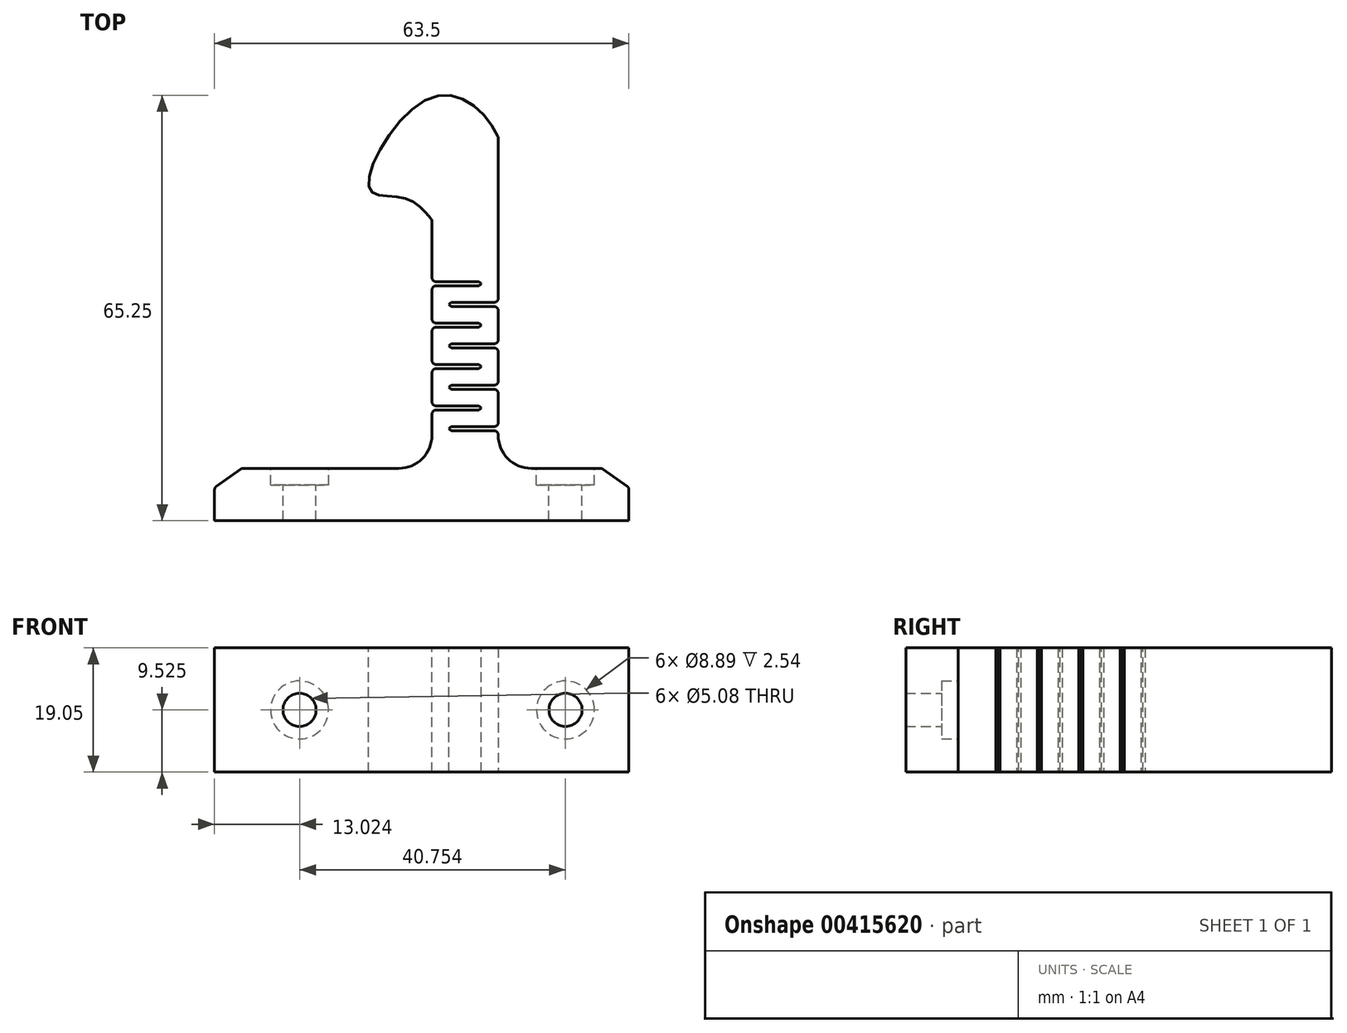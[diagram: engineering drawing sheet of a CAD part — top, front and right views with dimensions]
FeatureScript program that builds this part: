
annotation { "Feature Type Name" : "Feature", "Feature Type Description" : "" }
export const myFeature = defineFeature(function(context is Context, id is Id, definition is map)
    precondition{}
    {
        {
            var Q0;
            Q0=qCreatedBy(makeId("Top.planeOp"),FACE);
            var sketch = newSketch(context, id + "F0", { "sketchPlane" : qUnion([Q0])});
            skLineSegment(sketch, "E0", {"start": v(0, 0) * mm, "end": v(63.5, 0) * mm});
            skLineSegment(sketch, "E1", {"start": v(63.5, 0) * mm, "end": v(63.5, 5.08) * mm});
            skLineSegment(sketch, "E2", {"start": v(63.5, 5.08) * mm, "end": v(59.35, 8.01) * mm});
            skLineSegment(sketch, "E3", {"start": v(0, 0) * mm, "end": v(0, 5.08) * mm});
            skLineSegment(sketch, "E4", {"start": v(0, 5.08) * mm, "end": v(4.15, 8.01) * mm});
            skLineSegment(sketch, "E5", {"start": v(4.15, 8.01) * mm, "end": v(59.35, 8.01) * mm});
            skLineSegment(sketch, "E6", {"start": v(33.32, 8.01) * mm, "end": v(33.32, 46.11) * mm});
            skLineSegment(sketch, "E7", {"start": v(43.48, 8.01) * mm, "end": v(43.48, 58.81) * mm});
            skFitSpline(sketch, "E8", {"points": [v(33.32, 46.11) * mm, v(28.79, 49.55) * mm, v(23.73, 50.95) * mm, v(33.32, 64.92) * mm, v(43.48, 58.81) * mm, v(43.48, 47.98) * mm], "startDerivative": vector(-22.66, 29.78) * mm, "endDerivative": vector(-11.05, -50.67) * mm});
            skLineSegment(sketch, "E9.bottom", {"start": v(33.32, 36.01) * mm, "end": v(40.94, 36.01) * mm});
            skLineSegment(sketch, "E9.top", {"start": v(33.32, 36.65) * mm, "end": v(40.94, 36.65) * mm});
            skLineSegment(sketch, "E9.left", {"start": v(33.32, 36.01) * mm, "end": v(33.32, 36.65) * mm});
            skLineSegment(sketch, "E9.right", {"start": v(40.94, 36.01) * mm, "end": v(40.94, 36.65) * mm});
            skLineSegment(sketch, "E10", {"start": v(41.84, 33.47) * mm, "end": v(43.48, 33.47) * mm});
            skLineSegment(sketch, "E11.bottom", {"start": v(43.48, 33.47) * mm, "end": v(35.86, 33.47) * mm});
            skLineSegment(sketch, "E11.top", {"start": v(43.48, 32.84) * mm, "end": v(35.86, 32.84) * mm});
            skLineSegment(sketch, "E11.left", {"start": v(43.48, 33.47) * mm, "end": v(43.48, 32.84) * mm});
            skLineSegment(sketch, "E11.right", {"start": v(35.86, 33.47) * mm, "end": v(35.86, 32.84) * mm});
            skLineSegment(sketch, "E12", {"start": v(33.32, 36.01) * mm, "end": v(33.32, 30.3) * mm});
            skLineSegment(sketch, "E13", {"start": v(43.48, 32.84) * mm, "end": v(43.48, 27.12) * mm});
            skLineSegment(sketch, "E14.bottom", {"start": v(33.32, 30.3) * mm, "end": v(40.94, 30.3) * mm});
            skLineSegment(sketch, "E14.top", {"start": v(33.32, 29.66) * mm, "end": v(40.94, 29.66) * mm});
            skLineSegment(sketch, "E14.left", {"start": v(33.32, 30.3) * mm, "end": v(33.32, 29.66) * mm});
            skLineSegment(sketch, "E14.right", {"start": v(40.94, 30.3) * mm, "end": v(40.94, 29.66) * mm});
            skLineSegment(sketch, "E15.bottom", {"start": v(43.48, 27.12) * mm, "end": v(35.86, 27.12) * mm});
            skLineSegment(sketch, "E15.top", {"start": v(43.48, 26.49) * mm, "end": v(35.86, 26.49) * mm});
            skLineSegment(sketch, "E15.left", {"start": v(43.48, 27.12) * mm, "end": v(43.48, 26.49) * mm});
            skLineSegment(sketch, "E15.right", {"start": v(35.86, 27.12) * mm, "end": v(35.86, 26.49) * mm});
            skLineSegment(sketch, "E16", {"start": v(33.32, 29.66) * mm, "end": v(33.32, 23.95) * mm});
            skLineSegment(sketch, "E17", {"start": v(43.48, 26.49) * mm, "end": v(43.48, 20.77) * mm});
            skLineSegment(sketch, "E18.bottom", {"start": v(33.32, 23.95) * mm, "end": v(40.94, 23.95) * mm});
            skLineSegment(sketch, "E18.top", {"start": v(33.32, 23.31) * mm, "end": v(40.94, 23.31) * mm});
            skLineSegment(sketch, "E18.left", {"start": v(33.32, 23.95) * mm, "end": v(33.32, 23.31) * mm});
            skLineSegment(sketch, "E18.right", {"start": v(40.94, 23.95) * mm, "end": v(40.94, 23.31) * mm});
            skLineSegment(sketch, "E19.bottom", {"start": v(43.48, 20.77) * mm, "end": v(35.86, 20.77) * mm});
            skLineSegment(sketch, "E19.top", {"start": v(43.48, 20.14) * mm, "end": v(35.86, 20.14) * mm});
            skLineSegment(sketch, "E19.left", {"start": v(43.48, 20.77) * mm, "end": v(43.48, 20.14) * mm});
            skLineSegment(sketch, "E19.right", {"start": v(35.86, 20.77) * mm, "end": v(35.86, 20.14) * mm});
            skLineSegment(sketch, "E20", {"start": v(33.32, 23.31) * mm, "end": v(33.32, 17.6) * mm});
            skLineSegment(sketch, "E21", {"start": v(43.48, 20.14) * mm, "end": v(43.48, 14.42) * mm});
            skLineSegment(sketch, "E22.bottom", {"start": v(33.32, 17.6) * mm, "end": v(40.94, 17.6) * mm});
            skLineSegment(sketch, "E22.top", {"start": v(33.32, 16.96) * mm, "end": v(40.94, 16.96) * mm});
            skLineSegment(sketch, "E22.left", {"start": v(33.32, 17.6) * mm, "end": v(33.32, 16.96) * mm});
            skLineSegment(sketch, "E22.right", {"start": v(40.94, 17.6) * mm, "end": v(40.94, 16.96) * mm});
            skLineSegment(sketch, "E23.bottom", {"start": v(43.48, 14.42) * mm, "end": v(35.86, 14.42) * mm});
            skLineSegment(sketch, "E23.top", {"start": v(43.48, 13.79) * mm, "end": v(35.86, 13.79) * mm});
            skLineSegment(sketch, "E23.left", {"start": v(43.48, 14.42) * mm, "end": v(43.48, 13.79) * mm});
            skLineSegment(sketch, "E23.right", {"start": v(35.86, 14.42) * mm, "end": v(35.86, 13.79) * mm});
            skLineSegment(sketch, "E24", {"start": v(43.48, 36.01) * mm, "end": v(43.48, 33.47) * mm});
            skSolve(sketch);
        }
        {
            var Q0;
            Q0=makeQuery(id+"F0.imprint","IMPRINT",FACE,{"disambiguationData":[TD([[makeQuery(id+"F0.imprint","IMPRINT",EDGE,{"derivedFrom":sQuery(id+"F0.wireOp",EDGE,"E0")}),1.0]])]});
            var Q1;
            {var subQ0=sQuery(id+"F0.wireOp",EDGE,"E8");var subQ1=sQuery(id+"F0.wireOp",EDGE,"E7");var subQ2=makeQuery(id+"F0.imprint","INTERSECT",VERTEX,{"disambiguationData":[OD(0.0)],"derivedFrom":[subQ1,subQ0]});Q1=makeQuery(id+"F0.imprint","IMPRINT",FACE,{"disambiguationData":[TD([[makeQuery(id+"F0.imprint","IMPRINT",EDGE,{"disambiguationData":[TD([[subQ2,1.0]])],"derivedFrom":subQ1}),-1.0]])]});}
            var Q2;
            Q2=makeQuery(id+"F0.imprint","IMPRINT",FACE,{"disambiguationData":[TD([[makeQuery(id+"F0.imprint","IMPRINT",EDGE,{"derivedFrom":sQuery(id+"F0.wireOp",EDGE,"E9.bottom")}),-1.0]])]});
            extrude(context, id + "F1", {"entities" : qUnion([Q0, Q1, Q2]), "depth" : 19.05 * mm});
        }
        {
            var Q0;
            Q0=makeQuery(id+"F1.opExtrude","SWEPT_EDGE",EDGE,{"disambiguationData":[OSD([sQuery(id+"F0.wireOp",EDGE,"E5"),sQuery(id+"F0.wireOp",EDGE,"E6")])]});
            var Q1;
            Q1=makeQuery(id+"F1.opExtrude","SWEPT_EDGE",EDGE,{"disambiguationData":[OSD([sQuery(id+"F0.wireOp",EDGE,"E5"),sQuery(id+"F0.wireOp",EDGE,"E7")])]});
            fillet(context, id + "F2", {"entities" : qUnion([Q0, Q1]), "radius" : 5.08 * mm, "tangentPropagation" : true, "allowEdgeOverflow" : false});
        }
        {
            var Q0;
            {var subQ0=sQuery(id+"F0.wireOp",EDGE,"E5");Q0=makeQuery(id+"F1.opExtrude","SWEPT_FACE",FACE,{"disambiguationData":[OSD([subQ0]),TDD([makeQuery(id+"F0.imprint","IMPRINT",EDGE,{"disambiguationData":[TD([[makeQuery(id+"F0.imprint","INTERSECT",VERTEX,{"derivedFrom":[sQuery(id+"F0.wireOp",EDGE,"E4"),subQ0]}),-1.0]])],"derivedFrom":subQ0})])]});}
            var sketch = newSketch(context, id + "F3", { "sketchPlane" : qUnion([Q0])});
            skCircle(sketch, "E25", {"center": v(-13.02, 9.53) * mm, "radius": 2.54 * mm});
            skPoint(sketch, "E25.centerSnap0", {"position": v(-4.15, 9.53) * mm});
            skCircle(sketch, "E26", {"center": v(-13.02, 9.53) * mm, "radius": 4.45 * mm});
            skCircle(sketch, "E27", {"center": v(-53.78, 9.53) * mm, "radius": 2.54 * mm});
            skCircle(sketch, "E28", {"center": v(-53.78, 9.53) * mm, "radius": 4.45 * mm});
            skSolve(sketch);
        }
        {
            var Q0;
            Q0 = qSketchRegion(id + "F3", true);
            extrude(context, id + "F4", {"entities" : qUnion([Q0]), "operationType" : NewBodyOperationType.REMOVE, "oppositeDirection" : true, "depth" : 2.54 * mm});
        }
        {
            var Q0;
            {var subQ0=sQuery(id+"F0.wireOp",EDGE,"E5");Q0=makeQuery(id+"F4.boolean.opBoolean","SPLIT",FACE,{"disambiguationData":[TD([makeQuery(id+"F4.opExtrude","SWEPT_FACE",FACE,{"disambiguationData":[OSD([sQuery(id+"F3.wireOp",EDGE,"E25")])]})])],"derivedFrom":makeQuery(id+"F1.opExtrude","SWEPT_FACE",FACE,{"disambiguationData":[OSD([subQ0]),TDD([makeQuery(id+"F0.imprint","IMPRINT",EDGE,{"disambiguationData":[TD([[makeQuery(id+"F0.imprint","INTERSECT",VERTEX,{"derivedFrom":[sQuery(id+"F0.wireOp",EDGE,"E4"),subQ0]}),-1.0]])],"derivedFrom":subQ0})])]})});}
            var Q1;
            {var subQ0=sQuery(id+"F0.wireOp",EDGE,"E5");Q1=makeQuery(id+"F4.boolean.opBoolean","SPLIT",FACE,{"disambiguationData":[TD([makeQuery(id+"F4.opExtrude","SWEPT_FACE",FACE,{"disambiguationData":[OSD([sQuery(id+"F3.wireOp",EDGE,"E27")])]})])],"derivedFrom":makeQuery(id+"F1.opExtrude","SWEPT_FACE",FACE,{"disambiguationData":[OSD([subQ0]),TDD([makeQuery(id+"F0.imprint","IMPRINT",EDGE,{"disambiguationData":[TD([[makeQuery(id+"F0.imprint","INTERSECT",VERTEX,{"derivedFrom":[sQuery(id+"F0.wireOp",EDGE,"E2"),subQ0]}),1.0]])],"derivedFrom":subQ0})])]})});}
            extrude(context, id + "F5", {"entities" : qUnion([Q0, Q1]), "operationType" : NewBodyOperationType.REMOVE, "oppositeDirection" : true, "depth" : 25.4 * mm});
        }
        {
            var Q0;
            Q0=makeQuery(id+"F1.opExtrude","SWEPT_EDGE",EDGE,{"disambiguationData":[OSD([sQuery(id+"F0.wireOp",EDGE,"E21"),sQuery(id+"F0.wireOp",EDGE,"E23.bottom"),sQuery(id+"F0.wireOp",EDGE,"E23.left")])]});
            var Q1;
            Q1=makeQuery(id+"F1.opExtrude","SWEPT_EDGE",EDGE,{"disambiguationData":[OSD([sQuery(id+"F0.wireOp",EDGE,"E19.top"),sQuery(id+"F0.wireOp",EDGE,"E19.left"),sQuery(id+"F0.wireOp",EDGE,"E21")])]});
            var Q2;
            Q2=makeQuery(id+"F1.opExtrude","SWEPT_EDGE",EDGE,{"disambiguationData":[OSD([sQuery(id+"F0.wireOp",EDGE,"E17"),sQuery(id+"F0.wireOp",EDGE,"E19.bottom"),sQuery(id+"F0.wireOp",EDGE,"E19.left")])]});
            var Q3;
            Q3=makeQuery(id+"F1.opExtrude","SWEPT_EDGE",EDGE,{"disambiguationData":[OSD([sQuery(id+"F0.wireOp",EDGE,"E15.top"),sQuery(id+"F0.wireOp",EDGE,"E15.left"),sQuery(id+"F0.wireOp",EDGE,"E17")])]});
            var Q4;
            Q4=makeQuery(id+"F1.opExtrude","SWEPT_EDGE",EDGE,{"disambiguationData":[OSD([sQuery(id+"F0.wireOp",EDGE,"E13"),sQuery(id+"F0.wireOp",EDGE,"E15.bottom"),sQuery(id+"F0.wireOp",EDGE,"E15.left")])]});
            var Q5;
            Q5=makeQuery(id+"F1.opExtrude","SWEPT_EDGE",EDGE,{"disambiguationData":[OSD([sQuery(id+"F0.wireOp",EDGE,"E11.top"),sQuery(id+"F0.wireOp",EDGE,"E11.left"),sQuery(id+"F0.wireOp",EDGE,"E13")])]});
            var Q6;
            Q6=makeQuery(id+"F1.opExtrude","SWEPT_EDGE",EDGE,{"disambiguationData":[OSD([sQuery(id+"F0.wireOp",EDGE,"E7"),sQuery(id+"F0.wireOp",EDGE,"E11.bottom"),sQuery(id+"F0.wireOp",EDGE,"E11.left")])]});
            var Q7;
            Q7=makeQuery(id+"F1.opExtrude","SWEPT_EDGE",EDGE,{"disambiguationData":[OSD([sQuery(id+"F0.wireOp",EDGE,"E6"),sQuery(id+"F0.wireOp",EDGE,"E9.top"),sQuery(id+"F0.wireOp",EDGE,"E9.left")])]});
            var Q8;
            Q8=makeQuery(id+"F1.opExtrude","SWEPT_EDGE",EDGE,{"disambiguationData":[OSD([sQuery(id+"F0.wireOp",EDGE,"E9.bottom"),sQuery(id+"F0.wireOp",EDGE,"E9.left"),sQuery(id+"F0.wireOp",EDGE,"E12")])]});
            var Q9;
            Q9=makeQuery(id+"F1.opExtrude","SWEPT_EDGE",EDGE,{"disambiguationData":[OSD([sQuery(id+"F0.wireOp",EDGE,"E12"),sQuery(id+"F0.wireOp",EDGE,"E14.bottom"),sQuery(id+"F0.wireOp",EDGE,"E14.left")])]});
            var Q10;
            Q10=makeQuery(id+"F1.opExtrude","SWEPT_EDGE",EDGE,{"disambiguationData":[OSD([sQuery(id+"F0.wireOp",EDGE,"E14.top"),sQuery(id+"F0.wireOp",EDGE,"E14.left"),sQuery(id+"F0.wireOp",EDGE,"E16")])]});
            var Q11;
            Q11=makeQuery(id+"F1.opExtrude","SWEPT_EDGE",EDGE,{"disambiguationData":[OSD([sQuery(id+"F0.wireOp",EDGE,"E16"),sQuery(id+"F0.wireOp",EDGE,"E18.bottom"),sQuery(id+"F0.wireOp",EDGE,"E18.left")])]});
            var Q12;
            Q12=makeQuery(id+"F1.opExtrude","SWEPT_EDGE",EDGE,{"disambiguationData":[OSD([sQuery(id+"F0.wireOp",EDGE,"E18.top"),sQuery(id+"F0.wireOp",EDGE,"E18.left"),sQuery(id+"F0.wireOp",EDGE,"E20")])]});
            var Q13;
            Q13=makeQuery(id+"F1.opExtrude","SWEPT_EDGE",EDGE,{"disambiguationData":[OSD([sQuery(id+"F0.wireOp",EDGE,"E20"),sQuery(id+"F0.wireOp",EDGE,"E22.bottom"),sQuery(id+"F0.wireOp",EDGE,"E22.left")])]});
            var Q14;
            Q14=makeQuery(id+"F1.opExtrude","SWEPT_EDGE",EDGE,{"disambiguationData":[OSD([sQuery(id+"F0.wireOp",EDGE,"E6"),sQuery(id+"F0.wireOp",EDGE,"E22.top"),sQuery(id+"F0.wireOp",EDGE,"E22.left")])]});
            var Q15;
            Q15=makeQuery(id+"F1.opExtrude","SWEPT_EDGE",EDGE,{"disambiguationData":[OSD([sQuery(id+"F0.wireOp",EDGE,"E9.bottom"),sQuery(id+"F0.wireOp",EDGE,"E9.right")])]});
            var Q16;
            Q16=makeQuery(id+"F1.opExtrude","SWEPT_EDGE",EDGE,{"disambiguationData":[OSD([sQuery(id+"F0.wireOp",EDGE,"E14.top"),sQuery(id+"F0.wireOp",EDGE,"E14.right")])]});
            var Q17;
            Q17=makeQuery(id+"F1.opExtrude","SWEPT_EDGE",EDGE,{"disambiguationData":[OSD([sQuery(id+"F0.wireOp",EDGE,"E18.top"),sQuery(id+"F0.wireOp",EDGE,"E18.right")])]});
            var Q18;
            Q18=makeQuery(id+"F1.opExtrude","SWEPT_EDGE",EDGE,{"disambiguationData":[OSD([sQuery(id+"F0.wireOp",EDGE,"E22.top"),sQuery(id+"F0.wireOp",EDGE,"E22.right")])]});
            var Q19;
            Q19=makeQuery(id+"F1.opExtrude","SWEPT_EDGE",EDGE,{"disambiguationData":[OSD([sQuery(id+"F0.wireOp",EDGE,"E22.bottom"),sQuery(id+"F0.wireOp",EDGE,"E22.right")])]});
            var Q20;
            Q20=makeQuery(id+"F1.opExtrude","SWEPT_EDGE",EDGE,{"disambiguationData":[OSD([sQuery(id+"F0.wireOp",EDGE,"E18.bottom"),sQuery(id+"F0.wireOp",EDGE,"E18.right")])]});
            var Q21;
            Q21=makeQuery(id+"F1.opExtrude","SWEPT_EDGE",EDGE,{"disambiguationData":[OSD([sQuery(id+"F0.wireOp",EDGE,"E14.bottom"),sQuery(id+"F0.wireOp",EDGE,"E14.right")])]});
            var Q22;
            Q22=makeQuery(id+"F1.opExtrude","SWEPT_EDGE",EDGE,{"disambiguationData":[OSD([sQuery(id+"F0.wireOp",EDGE,"E9.top"),sQuery(id+"F0.wireOp",EDGE,"E9.right")])]});
            var Q23;
            Q23=makeQuery(id+"F1.opExtrude","SWEPT_EDGE",EDGE,{"disambiguationData":[OSD([sQuery(id+"F0.wireOp",EDGE,"E11.top"),sQuery(id+"F0.wireOp",EDGE,"E11.right")])]});
            var Q24;
            Q24=makeQuery(id+"F1.opExtrude","SWEPT_EDGE",EDGE,{"disambiguationData":[OSD([sQuery(id+"F0.wireOp",EDGE,"E15.top"),sQuery(id+"F0.wireOp",EDGE,"E15.right")])]});
            var Q25;
            Q25=makeQuery(id+"F1.opExtrude","SWEPT_EDGE",EDGE,{"disambiguationData":[OSD([sQuery(id+"F0.wireOp",EDGE,"E19.top"),sQuery(id+"F0.wireOp",EDGE,"E19.right")])]});
            var Q26;
            Q26=makeQuery(id+"F1.opExtrude","SWEPT_EDGE",EDGE,{"disambiguationData":[OSD([sQuery(id+"F0.wireOp",EDGE,"E23.top"),sQuery(id+"F0.wireOp",EDGE,"E23.right")])]});
            var Q27;
            Q27=makeQuery(id+"F1.opExtrude","SWEPT_EDGE",EDGE,{"disambiguationData":[OSD([sQuery(id+"F0.wireOp",EDGE,"E23.bottom"),sQuery(id+"F0.wireOp",EDGE,"E23.right")])]});
            var Q28;
            Q28=makeQuery(id+"F1.opExtrude","SWEPT_EDGE",EDGE,{"disambiguationData":[OSD([sQuery(id+"F0.wireOp",EDGE,"E19.bottom"),sQuery(id+"F0.wireOp",EDGE,"E19.right")])]});
            var Q29;
            Q29=makeQuery(id+"F1.opExtrude","SWEPT_EDGE",EDGE,{"disambiguationData":[OSD([sQuery(id+"F0.wireOp",EDGE,"E15.bottom"),sQuery(id+"F0.wireOp",EDGE,"E15.right")])]});
            var Q30;
            Q30=makeQuery(id+"F1.opExtrude","SWEPT_EDGE",EDGE,{"disambiguationData":[OSD([sQuery(id+"F0.wireOp",EDGE,"E11.bottom"),sQuery(id+"F0.wireOp",EDGE,"E11.right")])]});
            var Q31;
            Q31=makeQuery(id+"F1.opExtrude","SWEPT_EDGE",EDGE,{"disambiguationData":[OSD([sQuery(id+"F0.wireOp",EDGE,"E7"),sQuery(id+"F0.wireOp",EDGE,"E23.top"),sQuery(id+"F0.wireOp",EDGE,"E23.left")])]});
            var Q32;
            Q32=makeQuery(id+"F1.opExtrude","SWEPT_EDGE",EDGE,{"disambiguationData":[OSD([sQuery(id+"F0.wireOp",EDGE,"E6"),sQuery(id+"F0.wireOp",EDGE,"E8")])]});
            var Q33;
            Q33=makeQuery(id+"F1.opExtrude","SWEPT_EDGE",EDGE,{"disambiguationData":[OSD([sQuery(id+"F0.wireOp",EDGE,"E7"),sQuery(id+"F0.wireOp",EDGE,"E8")])]});
            var Q34;
            Q34=makeQuery(id+"F1.opExtrude","SWEPT_EDGE",EDGE,{"disambiguationData":[OSD([sQuery(id+"F0.wireOp",EDGE,"E2"),sQuery(id+"F0.wireOp",EDGE,"E5")])]});
            var Q35;
            Q35=makeQuery(id+"F1.opExtrude","SWEPT_EDGE",EDGE,{"disambiguationData":[OSD([sQuery(id+"F0.wireOp",EDGE,"E1"),sQuery(id+"F0.wireOp",EDGE,"E2")])]});
            var Q36;
            Q36=makeQuery(id+"F1.opExtrude","SWEPT_EDGE",EDGE,{"disambiguationData":[OSD([sQuery(id+"F0.wireOp",EDGE,"E3"),sQuery(id+"F0.wireOp",EDGE,"E4")])]});
            var Q37;
            Q37=makeQuery(id+"F1.opExtrude","SWEPT_EDGE",EDGE,{"disambiguationData":[OSD([sQuery(id+"F0.wireOp",EDGE,"E4"),sQuery(id+"F0.wireOp",EDGE,"E5")])]});
            fillet(context, id + "F6", {"entities" : qUnion([Q0, Q1, Q2, Q3, Q4, Q5, Q6, Q7, Q8, Q9, Q10, Q11, Q12, Q13, Q14, Q15, Q16, Q17, Q18, Q19, Q20, Q21, Q22, Q23, Q24, Q25, Q26, Q27, Q28, Q29, Q30, Q31, Q32, Q33, Q34, Q35, Q36, Q37]), "radius" : 0.64 * mm, "tangentPropagation" : true, "allowEdgeOverflow" : false});
        }
    });
